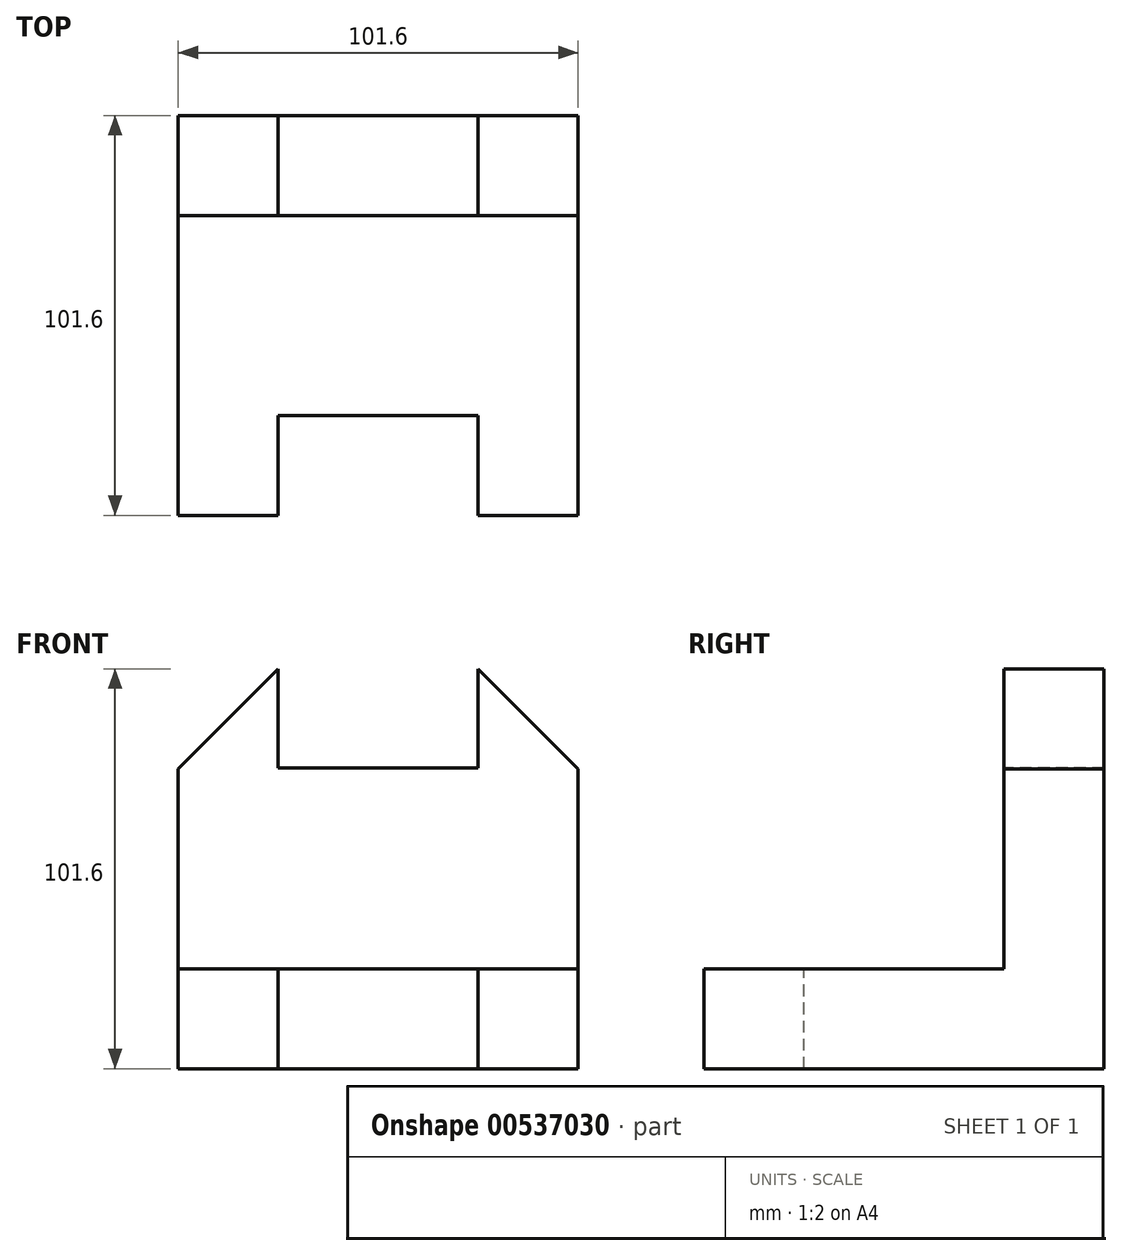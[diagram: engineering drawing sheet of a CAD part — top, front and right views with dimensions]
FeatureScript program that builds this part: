
annotation { "Feature Type Name" : "Feature", "Feature Type Description" : "" }
export const myFeature = defineFeature(function(context is Context, id is Id, definition is map)
    precondition{}
    {
        {
            var Q0;
            Q0=qCreatedBy(makeId("Front.planeOp"),FACE);
            var sketch = newSketch(context, id + "F0", { "sketchPlane" : qUnion([Q0])});
            skLineSegment(sketch, "E0.bottom", {"start": v(-56.62, 59.75) * mm, "end": v(44.98, 59.75) * mm});
            skLineSegment(sketch, "E0.top", {"start": v(-56.62, -41.85) * mm, "end": v(44.98, -41.85) * mm});
            skLineSegment(sketch, "E0.left", {"start": v(-56.62, 59.75) * mm, "end": v(-56.62, -41.85) * mm});
            skLineSegment(sketch, "E0.right", {"start": v(44.98, 59.75) * mm, "end": v(44.98, -41.85) * mm});
            skSolve(sketch);
        }
        {
            var Q0;
            Q0=qSketchRegion(id+"F0",true);
            extrude(context, id + "F1", {"entities" : qUnion([Q0]), "depth" : 101.6 * mm, "offsetDistance" : 25.4 * mm});
        }
        {
            var Q0;
            Q0=makeQuery(id+"F1.opExtrude","CAP_FACE",FACE,{"disambiguationData":[OSD([sQuery(id+"F0.wireOp",EDGE,"E0.bottom"),sQuery(id+"F0.wireOp",EDGE,"E0.top"),sQuery(id+"F0.wireOp",EDGE,"E0.left"),sQuery(id+"F0.wireOp",EDGE,"E0.right")])],"isStart":false});
            var sketch = newSketch(context, id + "F2", { "sketchPlane" : qUnion([Q0])});
            skLineSegment(sketch, "E1", {"start": v(-31.22, -41.85) * mm, "end": v(19.58, -41.85) * mm});
            skLineSegment(sketch, "E2", {"start": v(19.58, -41.85) * mm, "end": v(44.98, -41.85) * mm});
            skLineSegment(sketch, "E3", {"start": v(-31.22, -41.85) * mm, "end": v(-31.22, -16.45) * mm});
            skLineSegment(sketch, "E4", {"start": v(-31.22, -16.45) * mm, "end": v(19.58, -16.45) * mm});
            skLineSegment(sketch, "E5", {"start": v(19.58, -16.45) * mm, "end": v(19.58, -41.85) * mm});
            skSolve(sketch);
        }
        {
            var Q0;
            Q0=makeQuery(id+"F2.imprint","IMPRINT",FACE,{"disambiguationData":[TD([[makeQuery(id+"F2.imprint","IMPRINT",EDGE,{"derivedFrom":sQuery(id+"F2.wireOp",EDGE,"E1")}),1.0]])]});
            extrude(context, id + "F3", {"entities" : qUnion([Q0]), "operationType" : NewBodyOperationType.REMOVE, "oppositeDirection" : true, "depth" : 25.4 * mm, "offsetDistance" : 25.4 * mm});
        }
        {
            var Q0;
            Q0=makeQuery(id+"F1.opExtrude","CAP_FACE",FACE,{"disambiguationData":[OSD([sQuery(id+"F0.wireOp",EDGE,"E0.bottom"),sQuery(id+"F0.wireOp",EDGE,"E0.top"),sQuery(id+"F0.wireOp",EDGE,"E0.left"),sQuery(id+"F0.wireOp",EDGE,"E0.right")])],"isStart":false});
            var sketch = newSketch(context, id + "F4", { "sketchPlane" : qUnion([Q0])});
            skLineSegment(sketch, "E6.bottom", {"start": v(-56.62, -16.45) * mm, "end": v(44.98, -16.45) * mm});
            skLineSegment(sketch, "E6.top", {"start": v(-56.62, 59.75) * mm, "end": v(44.98, 59.75) * mm});
            skLineSegment(sketch, "E6.left", {"start": v(-56.62, -16.45) * mm, "end": v(-56.62, 59.75) * mm});
            skLineSegment(sketch, "E6.right", {"start": v(44.98, -16.45) * mm, "end": v(44.98, 59.75) * mm});
            skSolve(sketch);
        }
        {
            var Q0;
            Q0=qSketchRegion(id+"F4",true);
            extrude(context, id + "F5", {"entities" : qUnion([Q0]), "operationType" : NewBodyOperationType.REMOVE, "oppositeDirection" : true, "depth" : 76.2 * mm, "offsetDistance" : 25.4 * mm});
        }
        {
            var Q0;
            Q0=makeQuery(id+"F5.boolean.opBoolean","COPY",FACE,{"derivedFrom":makeQuery(id+"F5.opExtrude","CAP_FACE",FACE,{"disambiguationData":[OSD([sQuery(id+"F4.wireOp",EDGE,"E6.bottom"),sQuery(id+"F4.wireOp",EDGE,"E6.top"),sQuery(id+"F4.wireOp",EDGE,"E6.left"),sQuery(id+"F4.wireOp",EDGE,"E6.right")])],"isStart":false})});
            var sketch = newSketch(context, id + "F6", { "sketchPlane" : qUnion([Q0])});
            skLineSegment(sketch, "E7", {"start": v(-56.62, 59.75) * mm, "end": v(-31.22, 59.75) * mm});
            skLineSegment(sketch, "E8", {"start": v(-56.62, 59.75) * mm, "end": v(-56.62, 34.35) * mm});
            skLineSegment(sketch, "E9", {"start": v(-56.62, 34.35) * mm, "end": v(-31.22, 59.75) * mm});
            skLineSegment(sketch, "E10", {"start": v(19.58, 59.75) * mm, "end": v(44.98, 34.35) * mm});
            skLineSegment(sketch, "E11", {"start": v(44.98, 34.35) * mm, "end": v(44.98, 59.75) * mm});
            skLineSegment(sketch, "E12", {"start": v(44.98, 59.75) * mm, "end": v(19.58, 59.75) * mm});
            skSolve(sketch);
        }
        {
            var Q0;
            Q0=makeQuery(id+"F6.imprint","IMPRINT",FACE,{"disambiguationData":[TD([[makeQuery(id+"F6.imprint","IMPRINT",EDGE,{"derivedFrom":sQuery(id+"F6.wireOp",EDGE,"E10")}),1.0]])]});
            var Q1;
            Q1=makeQuery(id+"F6.imprint","IMPRINT",FACE,{"disambiguationData":[TD([[makeQuery(id+"F6.imprint","IMPRINT",EDGE,{"derivedFrom":sQuery(id+"F6.wireOp",EDGE,"E7")}),-1.0]])]});
            extrude(context, id + "F7", {"entities" : qUnion([Q0, Q1]), "operationType" : NewBodyOperationType.REMOVE, "oppositeDirection" : true, "depth" : 25.4 * mm, "offsetDistance" : 25.4 * mm});
        }
        {
            var Q0;
            Q0=makeQuery(id+"F5.boolean.opBoolean","COPY",FACE,{"derivedFrom":makeQuery(id+"F5.opExtrude","CAP_FACE",FACE,{"disambiguationData":[OSD([sQuery(id+"F4.wireOp",EDGE,"E6.bottom"),sQuery(id+"F4.wireOp",EDGE,"E6.top"),sQuery(id+"F4.wireOp",EDGE,"E6.left"),sQuery(id+"F4.wireOp",EDGE,"E6.right")])],"isStart":false})});
            var sketch = newSketch(context, id + "F8", { "sketchPlane" : qUnion([Q0])});
            skLineSegment(sketch, "E13.bottom", {"start": v(-31.22, 59.75) * mm, "end": v(19.58, 59.75) * mm});
            skLineSegment(sketch, "E13.top", {"start": v(-31.22, 8.95) * mm, "end": v(19.58, 8.95) * mm});
            skLineSegment(sketch, "E13.left", {"start": v(-31.22, 59.75) * mm, "end": v(-31.22, 8.95) * mm});
            skLineSegment(sketch, "E13.right", {"start": v(19.58, 59.75) * mm, "end": v(19.58, 8.95) * mm});
            skSolve(sketch);
        }
        {
            var Q0;
            Q0=makeQuery(id+"F8.imprint","IMPRINT",FACE,{"disambiguationData":[TD([[makeQuery(id+"F8.imprint","IMPRINT",EDGE,{"derivedFrom":sQuery(id+"F8.wireOp",EDGE,"E13.bottom")}),-1.0]])]});
            extrude(context, id + "F9", {"entities" : qUnion([Q0]), "operationType" : NewBodyOperationType.REMOVE, "oppositeDirection" : true, "depth" : 25.4 * mm, "offsetDistance" : 25.4 * mm});
        }
        {
            var Q0;
            Q0=makeQuery(id+"F9.boolean.opBoolean","COPY",FACE,{"derivedFrom":makeQuery(id+"F9.opExtrude","SWEPT_FACE",FACE,{"disambiguationData":[OSD([sQuery(id+"F8.wireOp",EDGE,"E13.top")])]})});
            extrude(context, id + "F10", {"entities" : qUnion([Q0]), "operationType" : NewBodyOperationType.ADD, "depth" : 50.8 * mm, "offsetDistance" : 25.4 * mm});
        }
        {
            var Q0;
            {var subQ0=sQuery(id+"F8.wireOp",EDGE,"E13.top");Q0=makeQuery(id+"F10.boolean.opBoolean","MERGE",FACE,{"derivedFrom":[makeQuery(id+"F5.boolean.opBoolean","COPY",FACE,{"derivedFrom":makeQuery(id+"F5.opExtrude","CAP_FACE",FACE,{"disambiguationData":[OSD([sQuery(id+"F4.wireOp",EDGE,"E6.bottom"),sQuery(id+"F4.wireOp",EDGE,"E6.top"),sQuery(id+"F4.wireOp",EDGE,"E6.left"),sQuery(id+"F4.wireOp",EDGE,"E6.right")])],"isStart":false})}),makeQuery(id+"F10.opExtrude","SWEPT_FACE",FACE,{"disambiguationData":[OSD([subQ0]),TDD([makeQuery(id+"F9.boolean.opBoolean","COPY",EDGE,{"derivedFrom":makeQuery(id+"F9.opExtrude","CAP_EDGE",EDGE,{"disambiguationData":[OSD([subQ0])],"isStart":true})})])]})]});}
            var sketch = newSketch(context, id + "F11", { "sketchPlane" : qUnion([Q0])});
            skLineSegment(sketch, "E14", {"start": v(-31.22, 59.75) * mm, "end": v(-31.22, 34.56) * mm});
            skLineSegment(sketch, "E15", {"start": v(-31.22, 34.56) * mm, "end": v(19.58, 34.56) * mm});
            skLineSegment(sketch, "E16", {"start": v(19.58, 34.56) * mm, "end": v(19.58, 59.75) * mm});
            skSolve(sketch);
        }
        {
            var Q0;
            Q0 = qSketchRegion(id + "F11", true);
            var Q1;
            Q1=makeQuery(id+"F11.imprint","IMPRINT",FACE,{"disambiguationData":[TD([[makeQuery(id+"F11.imprint","IMPRINT",EDGE,{"derivedFrom":sQuery(id+"F11.wireOp",EDGE,"E14")}),1.0]])]});
            extrude(context, id + "F12", {"entities" : qUnion([Q0, Q1]), "operationType" : NewBodyOperationType.REMOVE, "oppositeDirection" : true, "depth" : 59.44 * mm, "offsetDistance" : 25.4 * mm});
        }
    });
